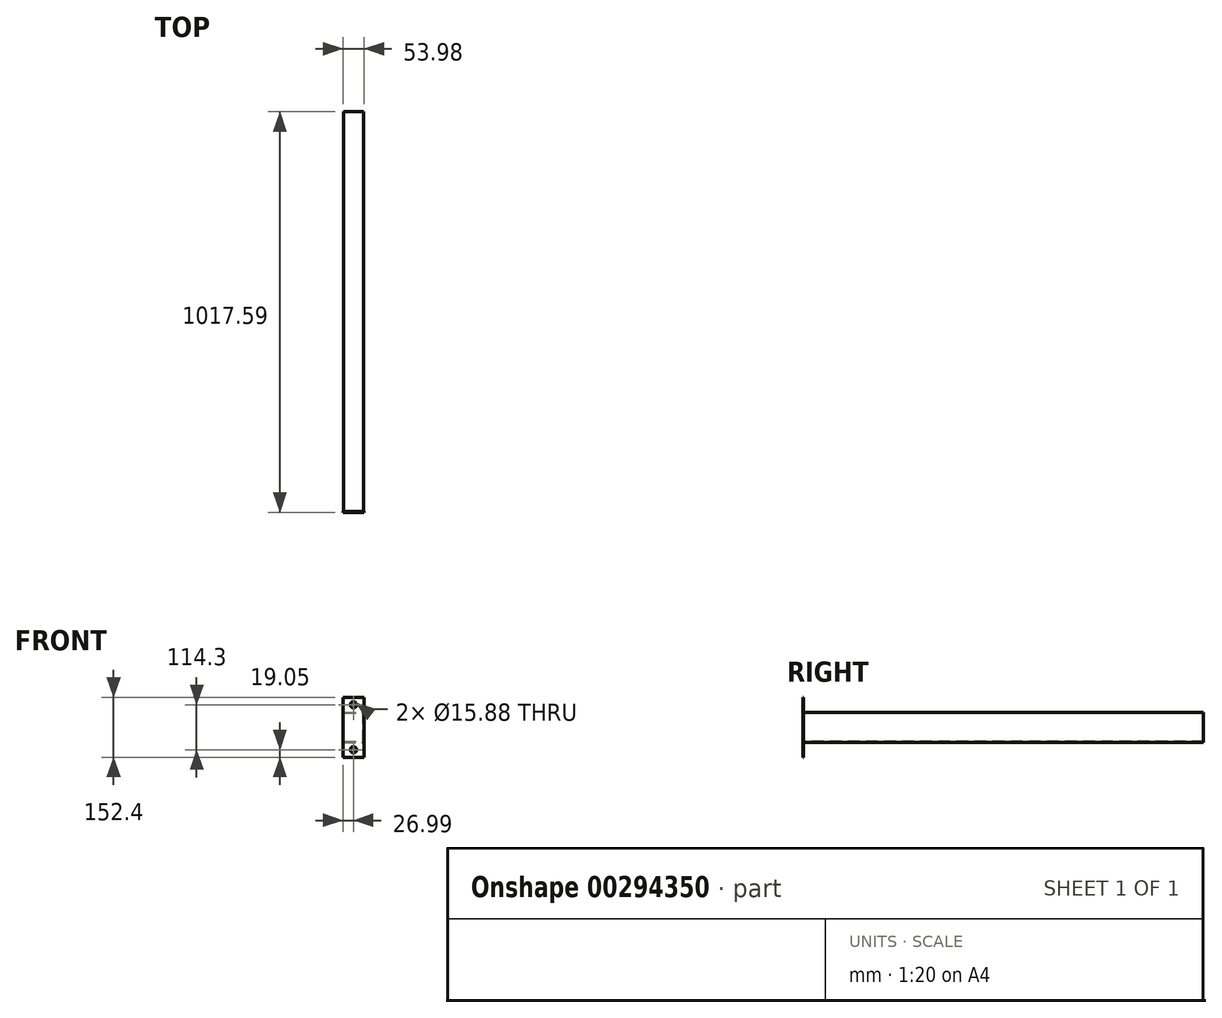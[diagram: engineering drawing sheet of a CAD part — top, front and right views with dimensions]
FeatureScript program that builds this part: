
annotation { "Feature Type Name" : "Feature", "Feature Type Description" : "" }
export const myFeature = defineFeature(function(context is Context, id is Id, definition is map)
    precondition{}
    {
        {
            var Q0;
            Q0=qCreatedBy(makeId("Front.planeOp"),FACE);
            var sketch = newSketch(context, id + "F0", { "sketchPlane" : qUnion([Q0])});
            skLineSegment(sketch, "E0.bottom", {"start": v(0, 0) * mm, "end": v(50.8, 0) * mm});
            skLineSegment(sketch, "E0.top", {"start": v(0, 76.2) * mm, "end": v(50.8, 76.2) * mm});
            skLineSegment(sketch, "E0.left", {"start": v(0, 0) * mm, "end": v(0, 76.2) * mm});
            skLineSegment(sketch, "E0.right", {"start": v(50.8, 0) * mm, "end": v(50.8, 76.2) * mm});
            skLineSegment(sketch, "E1.0", {"start": v(1.59, 74.61) * mm, "end": v(49.21, 74.61) * mm});
            skLineSegment(sketch, "E1.1", {"start": v(1.59, 1.59) * mm, "end": v(1.59, 74.61) * mm});
            skLineSegment(sketch, "E1.2", {"start": v(1.59, 1.59) * mm, "end": v(49.21, 1.59) * mm});
            skLineSegment(sketch, "E1.3", {"start": v(49.21, 1.59) * mm, "end": v(49.21, 74.61) * mm});
            skSolve(sketch);
        }
        {
            var Q0;
            Q0 = qSketchRegion(id + "F0", true);
            extrude(context, id + "F1", {"entities" : qUnion([Q0]), "oppositeDirection" : true, "depth" : 1016 * mm});
        }
        {
            var Q0;
            Q0=makeQuery(id+"F1.opExtrude","CAP_FACE",FACE,{"disambiguationData":[OSD([sQuery(id+"F0.wireOp",EDGE,"E0.bottom"),sQuery(id+"F0.wireOp",EDGE,"E0.top"),sQuery(id+"F0.wireOp",EDGE,"E0.left"),sQuery(id+"F0.wireOp",EDGE,"E0.right"),sQuery(id+"F0.wireOp",EDGE,"E1.0"),sQuery(id+"F0.wireOp",EDGE,"E1.1"),sQuery(id+"F0.wireOp",EDGE,"E1.2"),sQuery(id+"F0.wireOp",EDGE,"E1.3")])],"isStart":true});
            var sketch = newSketch(context, id + "F2", { "sketchPlane" : qUnion([Q0])});
            skLineSegment(sketch, "E2.bottom", {"start": v(-1.59, -38.1) * mm, "end": v(52.39, -38.1) * mm});
            skLineSegment(sketch, "E2.top", {"start": v(-1.59, 114.3) * mm, "end": v(52.39, 114.3) * mm});
            skLineSegment(sketch, "E2.left", {"start": v(-1.59, -38.1) * mm, "end": v(-1.59, 114.3) * mm});
            skLineSegment(sketch, "E2.right", {"start": v(52.39, -38.1) * mm, "end": v(52.39, 114.3) * mm});
            skLineSegment(sketch, "E3", {"start": v(1.59, 38.1) * mm, "end": v(49.21, 38.1) * mm, "construction": true});
            skLineSegment(sketch, "E4", {"start": v(-1.59, 38.1) * mm, "end": v(52.39, 38.1) * mm, "construction": true});
            skSolve(sketch);
        }
        {
            var Q0;
            Q0 = qSketchRegion(id + "F2", true);
            extrude(context, id + "F3", {"entities" : qUnion([Q0]), "operationType" : NewBodyOperationType.ADD, "depth" : 1.59 * mm});
        }
        {
            var Q0;
            Q0=makeQuery(id+"F3.opExtrude","CAP_FACE",FACE,{"disambiguationData":[OSD([sQuery(id+"F2.wireOp",EDGE,"E2.bottom"),sQuery(id+"F2.wireOp",EDGE,"E2.top"),sQuery(id+"F2.wireOp",EDGE,"E2.left"),sQuery(id+"F2.wireOp",EDGE,"E2.right")])],"isStart":false});
            var sketch = newSketch(context, id + "F4", { "sketchPlane" : qUnion([Q0])});
            skLineSegment(sketch, "E5", {"start": v(25.4, 114.3) * mm, "end": v(25.4, -38.1) * mm, "construction": true});
            skLineSegment(sketch, "E6", {"start": v(25.4, 95.25) * mm, "end": v(25.4, -19.05) * mm, "construction": true});
            skCircle(sketch, "E7", {"center": v(25.4, 95.25) * mm, "radius": 7.94 * mm});
            skCircle(sketch, "E8", {"center": v(25.4, -19.05) * mm, "radius": 7.94 * mm});
            skLineSegment(sketch, "E9", {"start": v(-1.59, 38.1) * mm, "end": v(52.39, 38.1) * mm, "construction": true});
            skPoint(sketch, "E10", {"position": v(25.4, 38.1) * mm});
            skSolve(sketch);
        }
        {
            var Q0;
            Q0 = qSketchRegion(id + "F4", true);
            var Q1;
            {var subQ0=sQuery(id+"F2.wireOp",EDGE,"E2.top");var subQ1=sQuery(id+"F2.wireOp",EDGE,"E2.left");var subQ2=sQuery(id+"F2.wireOp",EDGE,"E2.bottom");var subQ3=sQuery(id+"F2.wireOp",EDGE,"E2.right");Q1=makeQuery(id+"F3.boolean.opBoolean","SPLIT",FACE,{"disambiguationData":[TD([makeQuery(id+"F1.opExtrude","SWEPT_FACE",FACE,{"disambiguationData":[OSD([sQuery(id+"F0.wireOp",EDGE,"E0.bottom")])]})])],"derivedFrom":makeQuery(id+"F3.opExtrude","CAP_FACE",FACE,{"disambiguationData":[OSD([subQ2,subQ0,subQ1,subQ3])],"isStart":true})});}
            extrude(context, id + "F5", {"entities" : qUnion([Q0]), "operationType" : NewBodyOperationType.REMOVE, "endBound" : BoundingType.UP_TO_SURFACE, "oppositeDirection" : true, "endBoundEntityFace" : qUnion([Q1]), "depth" : 25.4 * mm});
        }
    });
